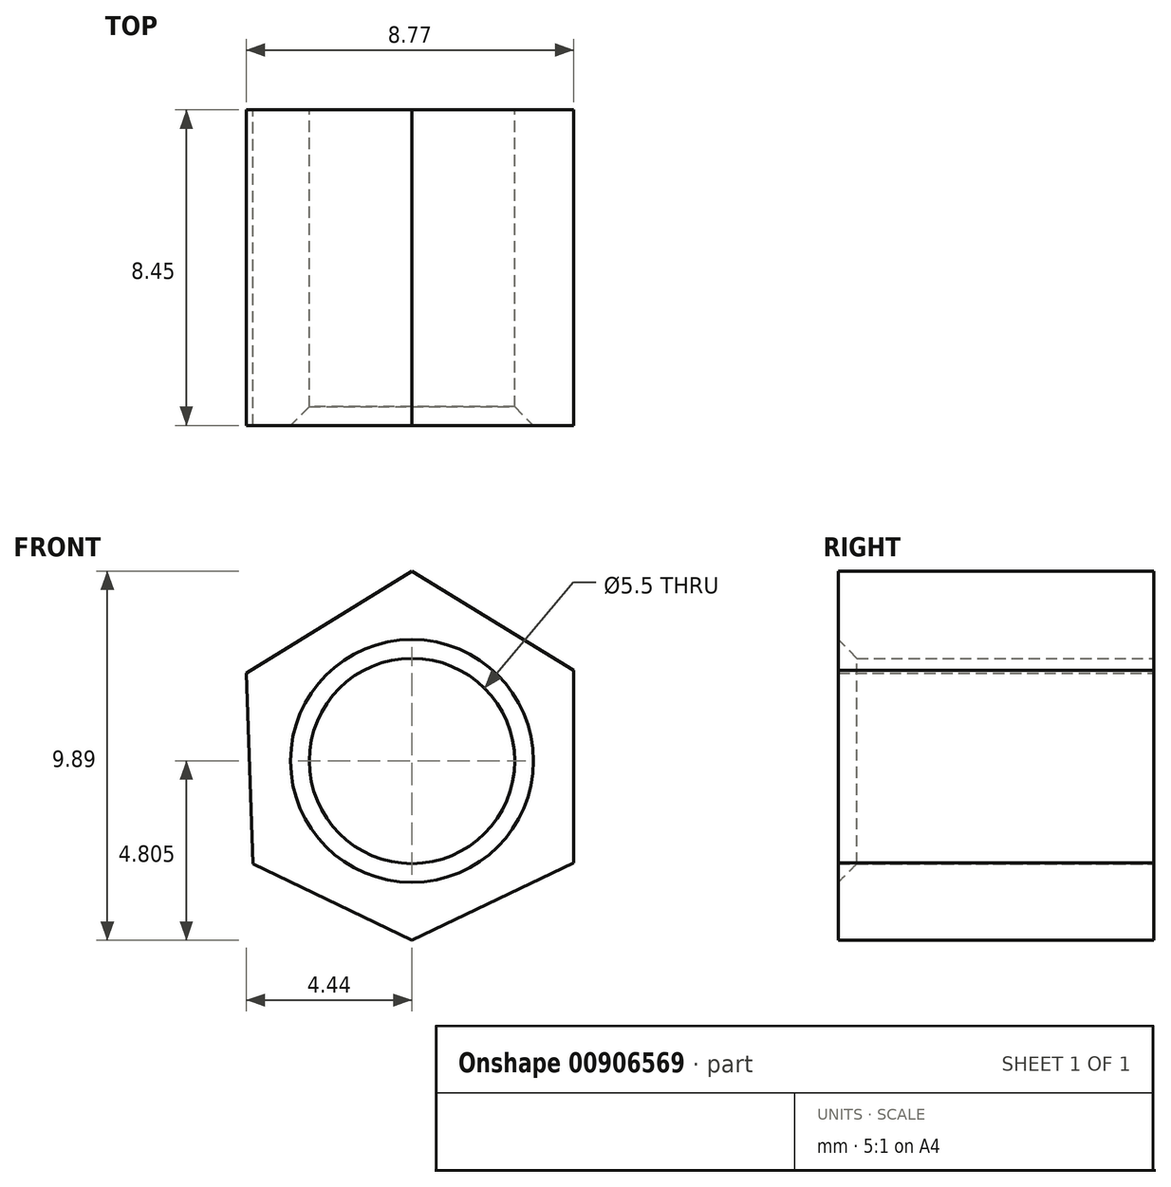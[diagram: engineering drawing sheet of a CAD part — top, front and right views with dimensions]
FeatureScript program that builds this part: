
annotation { "Feature Type Name" : "Feature", "Feature Type Description" : "" }
export const myFeature = defineFeature(function(context is Context, id is Id, definition is map)
    precondition{}
    {
        {
            var Q0;
            Q0=qCreatedBy(makeId("Front.planeOp"),FACE);
            var sketch = newSketch(context, id + "F0", { "sketchPlane" : qUnion([Q0])});
            skCircle(sketch, "E0", {"center": v(-134.7, 26.77) * mm, "radius": 4.33 * mm});
            skCircle(sketch, "E1", {"center": v(-134.7, 26.77) * mm, "radius": 2.75 * mm});
            skLineSegment(sketch, "E2", {"start": v(-139.15, 29.13) * mm, "end": v(-134.7, 31.86) * mm});
            skLineSegment(sketch, "E3", {"start": v(-134.7, 31.86) * mm, "end": v(-130.38, 29.2) * mm});
            skLineSegment(sketch, "E4", {"start": v(-130.38, 29.2) * mm, "end": v(-130.38, 24.05) * mm});
            skLineSegment(sketch, "E5", {"start": v(-130.38, 24.05) * mm, "end": v(-134.7, 21.97) * mm});
            skLineSegment(sketch, "E6", {"start": v(-134.7, 21.97) * mm, "end": v(-138.97, 24.02) * mm});
            skLineSegment(sketch, "E7", {"start": v(-139.15, 29.13) * mm, "end": v(-138.97, 24.02) * mm});
            skSolve(sketch);
        }
        {
            var Q0;
            Q0 = qSketchRegion(id + "F0", true);
            extrude(context, id + "F1", {"entities" : qUnion([Q0]), "depth" : 8.45 * mm, "offsetDistance" : 25.4 * mm});
        }
        {
            var Q0;
            Q0=makeQuery(id+"F1.opExtrude","CAP_EDGE",EDGE,{"disambiguationData":[OSD([sQuery(id+"F0.wireOp",EDGE,"E1")])],"isStart":false});
            chamfer(context, id + "F2", {"entities" : qUnion([Q0]), "width" : 0.5 * mm, "tangentPropagation" : true});
        }
    });
